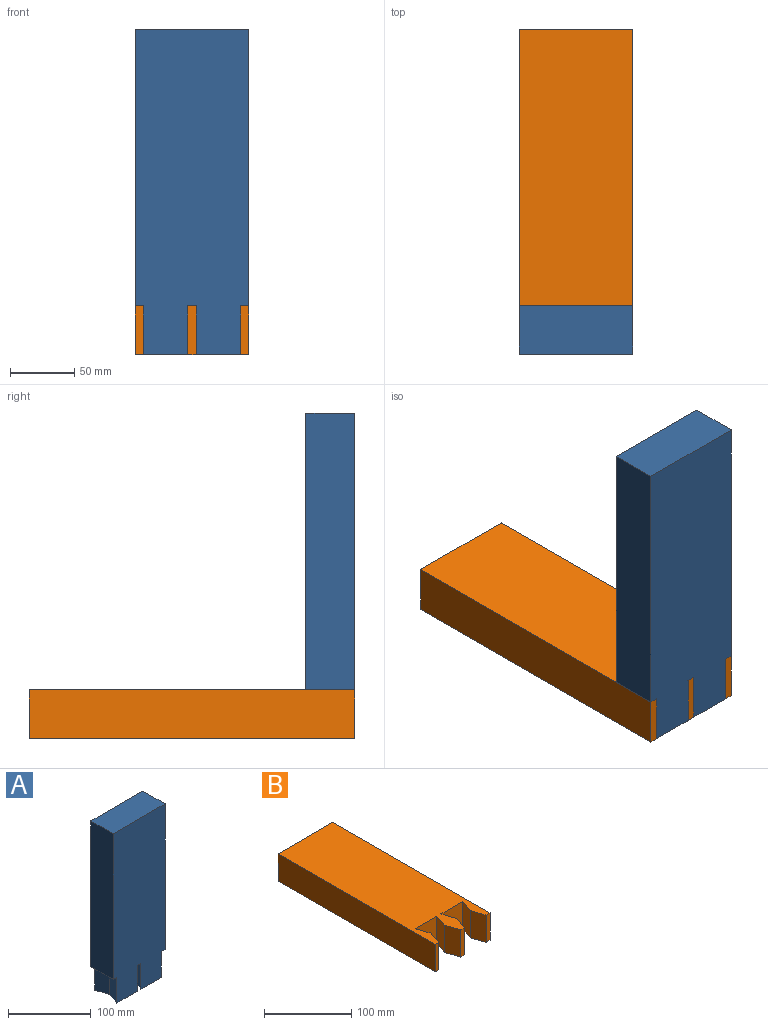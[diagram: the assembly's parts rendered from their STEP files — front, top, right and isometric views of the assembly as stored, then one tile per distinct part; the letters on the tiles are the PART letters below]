
ASSEMBLY  parts=2 mates=1
PART A: 18 faces, bbox 88.9x38.1x254 mm
  f0: plane 215.9x38.1mm, normal (-1,0,0), area 8225.8mm2, adj f4,f5,f6,f17
  f1: plane 38.1x34.93mm, normal (0,0,-1), area 1088.7mm2, adj f4,f5,f7,f8,f15,f16
  f2: plane 38.1x34.93mm, normal (0,0,-1), area 1088.7mm2, adj f4,f5,f9,f10,f12,f13
  f3: plane 215.9x38.1mm, normal (1,0,0), area 8225.8mm2, adj f4,f5,f6,f14
  f4: plane 254x88.9mm, normal (0,-1,0), area 21854.8mm2, adj f0,f1,f2,f3,f6,f7,f10,f11
  f5: plane 254x88.9mm, normal (0,1,0), area 21854.8mm2, adj f0,f1,f2,f3,f6,f8,f9,f11
  f6: plane 88.9x38.1mm, normal (0,0,1), area 3387.1mm2, adj f0,f3,f4,f5
  f7: plane 38.1x19.05mm, normal (0.95,0.32,0), area 765.1mm2, adj f1,f4,f8,f11
  f8: plane 38.1x19.05mm, normal (0.95,-0.32,0), area 765.1mm2, adj f1,f5,f7,f11
  f9: plane 38.1x19.05mm, normal (-0.95,-0.32,0), area 765.1mm2, adj f2,f5,f10,f11
  f10: plane 38.1x19.05mm, normal (-0.95,0.32,0), area 765.1mm2, adj f2,f4,f9,f11
  f11: plane 38.1x19.05mm, normal (0,0,-1), area 483.9mm2, adj f4,f5,f7,f8,f9,f10
  f12: plane 38.1x19.05mm, normal (0.95,0.32,0), area 765.1mm2, adj f2,f4,f13,f14
  f13: plane 38.1x19.05mm, normal (0.95,-0.32,0), area 765.1mm2, adj f2,f5,f12,f14
  f14: plane 38.1x12.7mm, normal (0,0,-1), area 362.9mm2, adj f3,f4,f5,f12,f13
  f15: plane 38.1x19.05mm, normal (-0.95,-0.32,0), area 765.1mm2, adj f1,f5,f16,f17
  f16: plane 38.1x19.05mm, normal (-0.95,0.32,0), area 765.1mm2, adj f1,f4,f15,f17
  f17: plane 38.1x12.7mm, normal (0,0,-1), area 362.9mm2, adj f0,f4,f5,f15,f16
PART B: 18 faces, bbox 88.9x254x38.1 mm
  f0: plane 38.1x6.35mm, normal (0,-1,0), area 241.9mm2, adj f2,f3,f9,f13
  f1: plane 38.1x6.35mm, normal (0,-1,0), area 241.9mm2, adj f2,f3,f7,f10
  f2: plane 254x88.9mm, normal (0,0,1), area 20403.2mm2, adj f0,f1,f4,f5,f6,f7,f8,f9
  f3: plane 254x88.9mm, normal (0,0,-1), area 20403.2mm2, adj f0,f1,f4,f5,f6,f7,f8,f9
  f4: plane 88.9x38.1mm, normal (0,1,0), area 3387.1mm2, adj f2,f3,f5,f7
  f5: plane 254x38.1mm, normal (-1,0,0), area 9677.4mm2, adj f2,f3,f4,f6
  f6: plane 38.1x6.35mm, normal (0,-1,0), area 241.9mm2, adj f2,f3,f5,f17
  f7: plane 254x38.1mm, normal (1,0,0), area 9677.4mm2, adj f1,f2,f3,f4
  f8: plane 38.1x19.05mm, normal (0.95,0.32,0), area 765.1mm2, adj f2,f3,f9,f12
  f9: plane 38.1x19.05mm, normal (0.95,-0.32,0), area 765.1mm2, adj f0,f2,f3,f8
  f10: plane 38.1x19.05mm, normal (-0.95,-0.32,0), area 765.1mm2, adj f1,f2,f3,f11
  f11: plane 38.1x19.05mm, normal (-0.95,0.32,0), area 765.1mm2, adj f2,f3,f10,f12
  f12: plane 38.1x34.93mm, normal (0,-1,0), area 1330.6mm2, adj f2,f3,f8,f11
  f13: plane 38.1x19.05mm, normal (-0.95,-0.32,0), area 765.1mm2, adj f0,f2,f3,f14
  f14: plane 38.1x19.05mm, normal (-0.95,0.32,0), area 765.1mm2, adj f2,f3,f13,f15
  f15: plane 38.1x34.93mm, normal (0,-1,0), area 1330.6mm2, adj f2,f3,f14,f16
  f16: plane 38.1x19.05mm, normal (0.95,0.32,0), area 765.1mm2, adj f2,f3,f15,f17
  f17: plane 38.1x19.05mm, normal (0.95,-0.32,0), area 765.1mm2, adj f2,f3,f6,f16
PLACE A t=(-117.47,-37.7,53.84)mm
PLACE B t=(-122.71,57.89,-85.2)mm
MATE fastened B.f12 <-> A.f5  axis (0,-1,0) through (-125.92,-37.7,-85.2)mm
